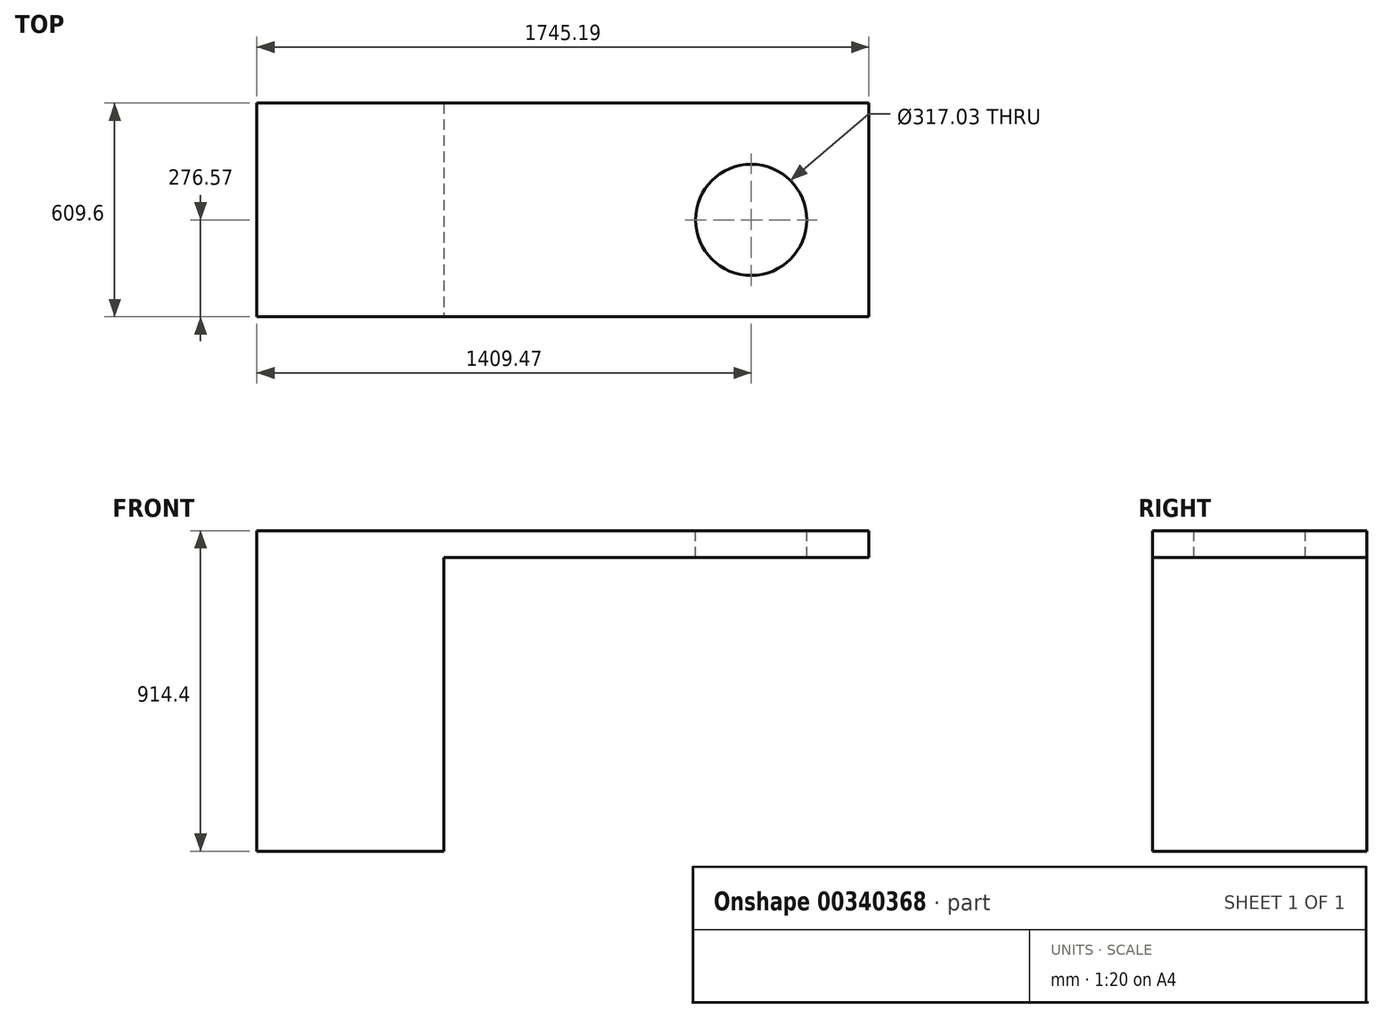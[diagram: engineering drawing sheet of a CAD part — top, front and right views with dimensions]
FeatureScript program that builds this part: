
annotation { "Feature Type Name" : "Feature", "Feature Type Description" : "" }
export const myFeature = defineFeature(function(context is Context, id is Id, definition is map)
    precondition{}
    {
        {
            var Q0;
            Q0=qCreatedBy(makeId("Front.planeOp"),FACE);
            var sketch = newSketch(context, id + "F0", { "sketchPlane" : qUnion([Q0])});
            skLineSegment(sketch, "E0.bottom", {"start": v(-266.7, 457.2) * mm, "end": v(266.7, 457.2) * mm});
            skLineSegment(sketch, "E0.top", {"start": v(-266.7, -457.2) * mm, "end": v(266.7, -457.2) * mm});
            skLineSegment(sketch, "E0.left", {"start": v(-266.7, 457.2) * mm, "end": v(-266.7, -457.2) * mm});
            skLineSegment(sketch, "E0.right", {"start": v(266.7, 457.2) * mm, "end": v(266.7, -457.2) * mm});
            skPoint(sketch, "E0.middle", {"position": v(0, 0) * mm});
            skSolve(sketch);
        }
        {
            var Q0;
            Q0 = qSketchRegion(id + "F0", true);
            extrude(context, id + "F1", {"entities" : qUnion([Q0]), "oppositeDirection" : true, "depth" : 609.6 * mm});
        }
        {
            var Q0;
            Q0=makeQuery(id+"F1.opExtrude","SWEPT_FACE",FACE,{"disambiguationData":[OSD([sQuery(id+"F0.wireOp",EDGE,"E0.bottom")])]});
            var sketch = newSketch(context, id + "F2", { "sketchPlane" : qUnion([Q0])});
            skLineSegment(sketch, "E1.bottom", {"start": v(266.7, 609.6) * mm, "end": v(1478.49, 609.6) * mm});
            skLineSegment(sketch, "E1.top", {"start": v(266.7, 0) * mm, "end": v(1478.49, 0) * mm});
            skLineSegment(sketch, "E1.left", {"start": v(266.7, 609.6) * mm, "end": v(266.7, 0) * mm});
            skLineSegment(sketch, "E1.right", {"start": v(1478.49, 609.6) * mm, "end": v(1478.49, 0) * mm});
            skSolve(sketch);
        }
        {
            var Q0;
            Q0 = qSketchRegion(id + "F2", true);
            extrude(context, id + "F3", {"entities" : qUnion([Q0]), "operationType" : NewBodyOperationType.ADD, "oppositeDirection" : true, "depth" : 76.2 * mm});
        }
        {
            var Q0;
            Q0=makeQuery(id+"F3.boolean.opBoolean","MERGE",FACE,{"derivedFrom":[makeQuery(id+"F1.opExtrude","SWEPT_FACE",FACE,{"disambiguationData":[OSD([sQuery(id+"F0.wireOp",EDGE,"E0.bottom")])]}),makeQuery(id+"F3.opExtrude","CAP_FACE",FACE,{"disambiguationData":[OSD([sQuery(id+"F2.wireOp",EDGE,"E1.bottom"),sQuery(id+"F2.wireOp",EDGE,"E1.top"),sQuery(id+"F2.wireOp",EDGE,"E1.left"),sQuery(id+"F2.wireOp",EDGE,"E1.right")])],"isStart":true})]});
            var sketch = newSketch(context, id + "F4", { "sketchPlane" : qUnion([Q0])});
            skCircle(sketch, "E2", {"center": v(1142.77, 276.57) * mm, "radius": 158.51 * mm});
            skSolve(sketch);
        }
        {
            var Q0;
            Q0 = qSketchRegion(id + "F4", true);
            extrude(context, id + "F5", {"entities" : qUnion([Q0]), "operationType" : NewBodyOperationType.REMOVE, "endBound" : BoundingType.THROUGH_ALL, "oppositeDirection" : true, "depth" : 25.4 * mm});
        }
    });
